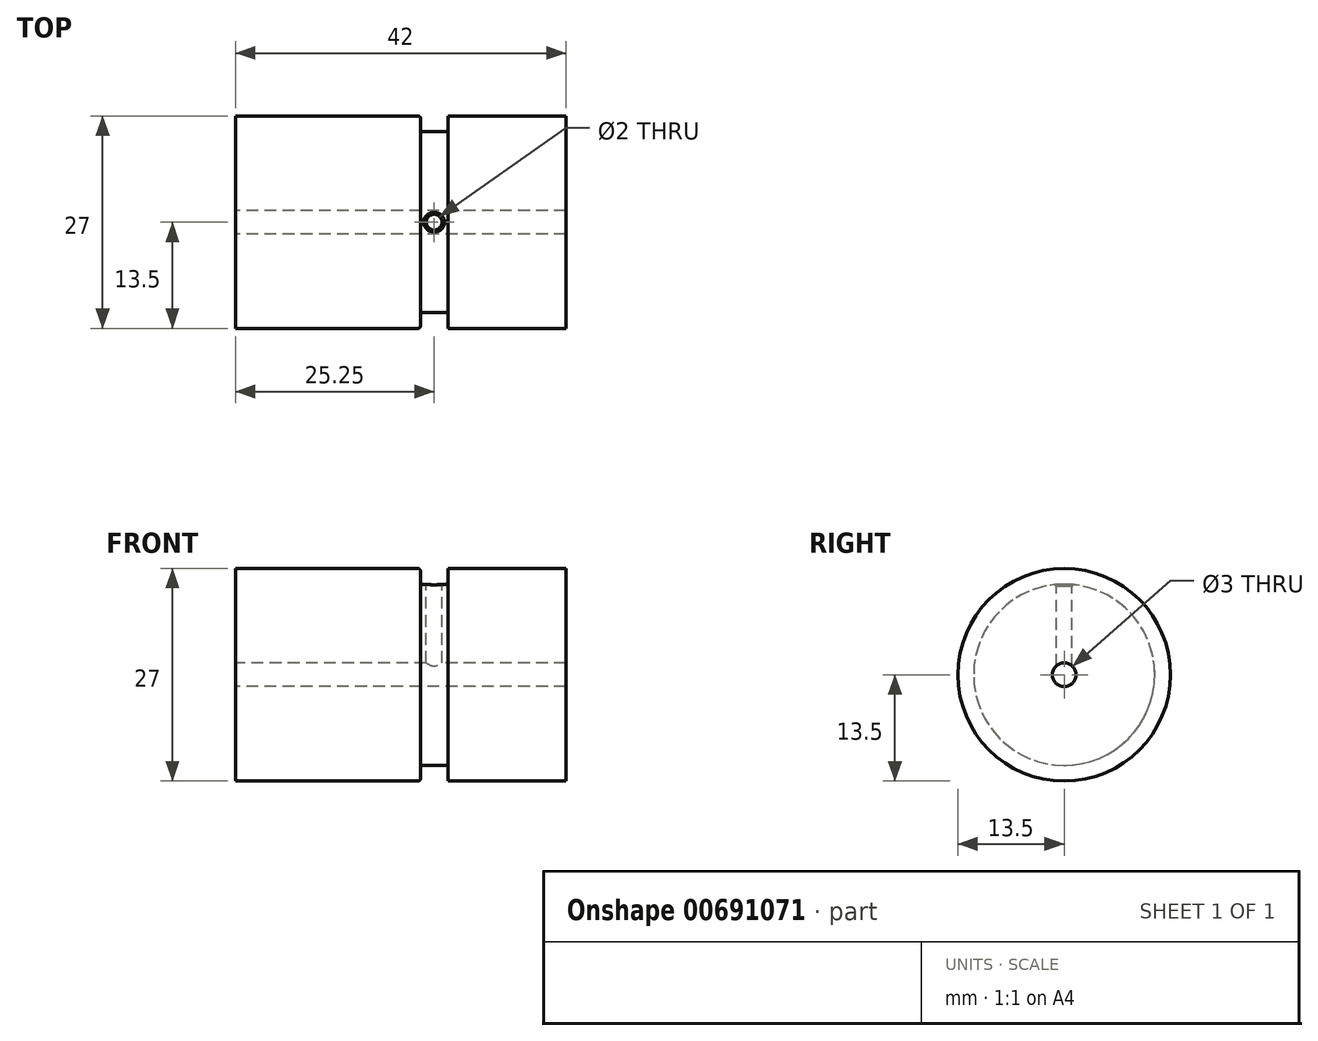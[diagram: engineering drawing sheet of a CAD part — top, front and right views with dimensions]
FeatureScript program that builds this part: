
annotation { "Feature Type Name" : "Feature", "Feature Type Description" : "" }
export const myFeature = defineFeature(function(context is Context, id is Id, definition is map)
    precondition{}
    {
        {
            var Q0;
            Q0=qCreatedBy(makeId("Front.planeOp"),FACE);
            var sketch = newSketch(context, id + "F0", { "sketchPlane" : qUnion([Q0])});
            skLineSegment(sketch, "E0.bottom", {"start": v(-42, 13.5) * mm, "end": v(0, 13.5) * mm});
            skLineSegment(sketch, "E0.top", {"start": v(-42, 1.5) * mm, "end": v(0, 1.5) * mm});
            skLineSegment(sketch, "E0.left", {"start": v(-42, 13.5) * mm, "end": v(-42, 1.5) * mm});
            skLineSegment(sketch, "E0.right", {"start": v(0, 13.5) * mm, "end": v(0, 1.5) * mm});
            skLineSegment(sketch, "E1", {"start": v(-16.04, 0) * mm, "end": v(-4.5, 0) * mm, "construction": true});
            skSolve(sketch);
        }
        {
            var Q0;
            Q0=makeQuery(id+"F0.imprint","IMPRINT",FACE,{"disambiguationData":[TD([[makeQuery(id+"F0.imprint","IMPRINT",EDGE,{"derivedFrom":sQuery(id+"F0.wireOp",EDGE,"E0.bottom")}),-1.0]])]});
            var Q1;
            Q1=sQuery(id+"F0.wireOp",EDGE,"E0.bottom");
            var Q2;
            Q2=sQuery(id+"F0.wireOp",EDGE,"E0.top");
            var Q3;
            Q3=sQuery(id+"F0.wireOp",EDGE,"E0.left");
            var Q4;
            Q4=sQuery(id+"F0.wireOp",EDGE,"E0.right");
            var Q5;
            Q5=sQuery(id+"F0.wireOp",EDGE,"E1");
            revolve(context, id + "F1", {"entities" : qUnion([Q0]), "surfaceEntities" : qUnion([Q1, Q2, Q3, Q4]), "axis" : qUnion([Q5]), "revolveType" : RevolveType.FULL});
        }
        {
            var Q0;
            Q0 = qSketchRegion(id + "F0", true);
            var sketch = newSketch(context, id + "F2", { "sketchPlane" : qUnion([Q0])});
            skLineSegment(sketch, "E2", {"start": v(-18.5, 11.5) * mm, "end": v(-18.5, 13.5) * mm});
            skLineSegment(sketch, "E3", {"start": v(-18.5, 13.5) * mm, "end": v(-15, 13.5) * mm});
            skLineSegment(sketch, "E4", {"start": v(-15, 13.5) * mm, "end": v(-15, 11.5) * mm});
            skLineSegment(sketch, "E5", {"start": v(-18.5, 11.5) * mm, "end": v(-15, 11.5) * mm});
            skLineSegment(sketch, "E6", {"start": v(0, 0) * mm, "end": v(-42, 0) * mm, "construction": true});
            skPoint(sketch, "E7.start.orphan", {"position": v(-42, 0) * mm});
            skSolve(sketch);
        }
        {
            var Q0;
            Q0 = qSketchRegion(id + "F2", true);
            var Q1;
            Q1=sQuery(id+"F2.wireOp",EDGE,"E6");
            revolve(context, id + "F3", {"operationType" : NewBodyOperationType.REMOVE, "entities" : qUnion([Q0]), "axis" : qUnion([Q1]), "revolveType" : RevolveType.FULL, "oppositeDirection" : true});
        }
        {
            var Q0;
            Q0=makeQuery(id+"F3.boolean.opBoolean","COPY",EDGE,{"derivedFrom":makeQuery(id+"F3.opRevolve","SWEPT_EDGE",EDGE,{"disambiguationData":[OSD([sQuery(id+"F0.wireOp",EDGE,"E0.bottom"),sQuery(id+"F2.wireOp",EDGE,"E2"),sQuery(id+"F2.wireOp",EDGE,"E3")])]})});
            var Q1;
            Q1=makeQuery(id+"F3.boolean.opBoolean","COPY",EDGE,{"derivedFrom":makeQuery(id+"F3.opRevolve","SWEPT_EDGE",EDGE,{"disambiguationData":[OSD([sQuery(id+"F0.wireOp",EDGE,"E0.bottom"),sQuery(id+"F2.wireOp",EDGE,"E3"),sQuery(id+"F2.wireOp",EDGE,"E4")])]})});
            var Q2;
            Q2=makeQuery(id+"F3.boolean.opBoolean","COPY",EDGE,{"derivedFrom":makeQuery(id+"F3.opRevolve","SWEPT_EDGE",EDGE,{"disambiguationData":[OSD([sQuery(id+"F2.wireOp",EDGE,"E2"),sQuery(id+"F2.wireOp",EDGE,"E5")])]})});
            var Q3;
            Q3=makeQuery(id+"F3.boolean.opBoolean","COPY",EDGE,{"derivedFrom":makeQuery(id+"F3.opRevolve","SWEPT_EDGE",EDGE,{"disambiguationData":[OSD([sQuery(id+"F2.wireOp",EDGE,"E4"),sQuery(id+"F2.wireOp",EDGE,"E5")])]})});
            fillet(context, id + "F4", {"entities" : qUnion([Q0, Q1, Q2, Q3]), "radius" : 0.3 * mm, "tangentPropagation" : true, "allowEdgeOverflow" : false});
        }
        {
            var Q0;
            Q0 = qSketchRegion(id + "F2", true);
            var sketch = newSketch(context, id + "F5", { "sketchPlane" : qUnion([Q0])});
            skLineSegment(sketch, "E8", {"start": v(-16.75, 11.5) * mm, "end": v(-16.75, 9.5) * mm, "construction": true});
            skLineSegment(sketch, "E9", {"start": v(-16.75, 11.5) * mm, "end": v(-15.4, 11.5) * mm});
            skLineSegment(sketch, "E10", {"start": v(-15.4, 11.5) * mm, "end": v(-15.4, 11.5) * mm});
            skLineSegment(sketch, "E11", {"start": v(-15.75, 11.3) * mm, "end": v(-15.75, 0) * mm});
            skLineSegment(sketch, "E12", {"start": v(-15.4, 11.5) * mm, "end": v(-15.75, 11.3) * mm});
            skLineSegment(sketch, "E13", {"start": v(-15.75, 0) * mm, "end": v(-16.75, 0) * mm});
            skLineSegment(sketch, "E14", {"start": v(-16.75, 0) * mm, "end": v(-16.75, 11.5) * mm});
            skSolve(sketch);
        }
        {
            var Q0;
            Q0 = qSketchRegion(id + "F5", true);
            var Q1;
            Q1=sQuery(id+"F5.wireOp",EDGE,"E14");
            revolve(context, id + "F6", {"operationType" : NewBodyOperationType.REMOVE, "entities" : qUnion([Q0]), "axis" : qUnion([Q1]), "revolveType" : RevolveType.FULL, "oppositeDirection" : true});
        }
    });
